# Revit family: WL2082 Native
name_source: partatom
category: Communication Devices
revit_build: Autodesk Revit Architecture 2012 (Build: 20110309_2315(x64)
units: mm (PartAtom-declared; Revit-internal decimal feet)

## types (1)
- WL2082 Native
    Coverage Horizontal = 140.00°
    Coverage Vertical = 10.00°
    Depth = 13.388"
    Description = Dual 8" Line Array Loudspeaker Element
    Enclosure Finish = Black Finish
    Enclosure Front Offset = 1.776"
    Enclosure Height = 10.150"
    Enclosure Rear Offset = 11.461"
    Fly Hardware Finish = Black Finish
    Grille Finish = Black Grille
    Height = 11.840"
    Impedance = 16
    Impedance 2 = 16
    Impedance 3 = 16
    Inner Width = 26.196"
    Interior Monolith Front Setback = 4.000"
    Interior Monolith Height = 7.761"
    Interior Monolith Rear Setback = 10.433"
    Manufacturer = QSC Audio Products, LLC
    Manufacturer URL = www.qscaudio.com
    Model = ILA WL2082-i
    Negative Rear Opening Depth = -1.500"
    Outer Width = 27.030"
    Power Handling = 400
    Power Handling 2 = 400
    Power Handling 3 = 200
    Product Documentation Link = http://media.qscaudio.com
    Product Page URL = http://www.qscaudio.com
    Rear Opening Depth = 1.500"
    Rear Opening Height = 4.400"
    Rear Opening Width = 8.000"
    Regulatory Compliance = RoHS
    Rigging Panel Depth = 12.272"
    Rigging Panel Front Setback = 1.116"
    Rigging Panel Height = 11.840"
    Rigging Panel Rear Setback = 13.388"
    Rotation Axis Distance = 82.419"
    SPL Max = 126
    Sensitivity = 96
    Sensitivity 2 = 96
    Sensitivity 3 = 106
    URL = http://www.qscaudio.com
    Width = 27.030"

## geometry (parser evidence)
native form markers: Sweep x1
no freeform markers — native parametric forms only
